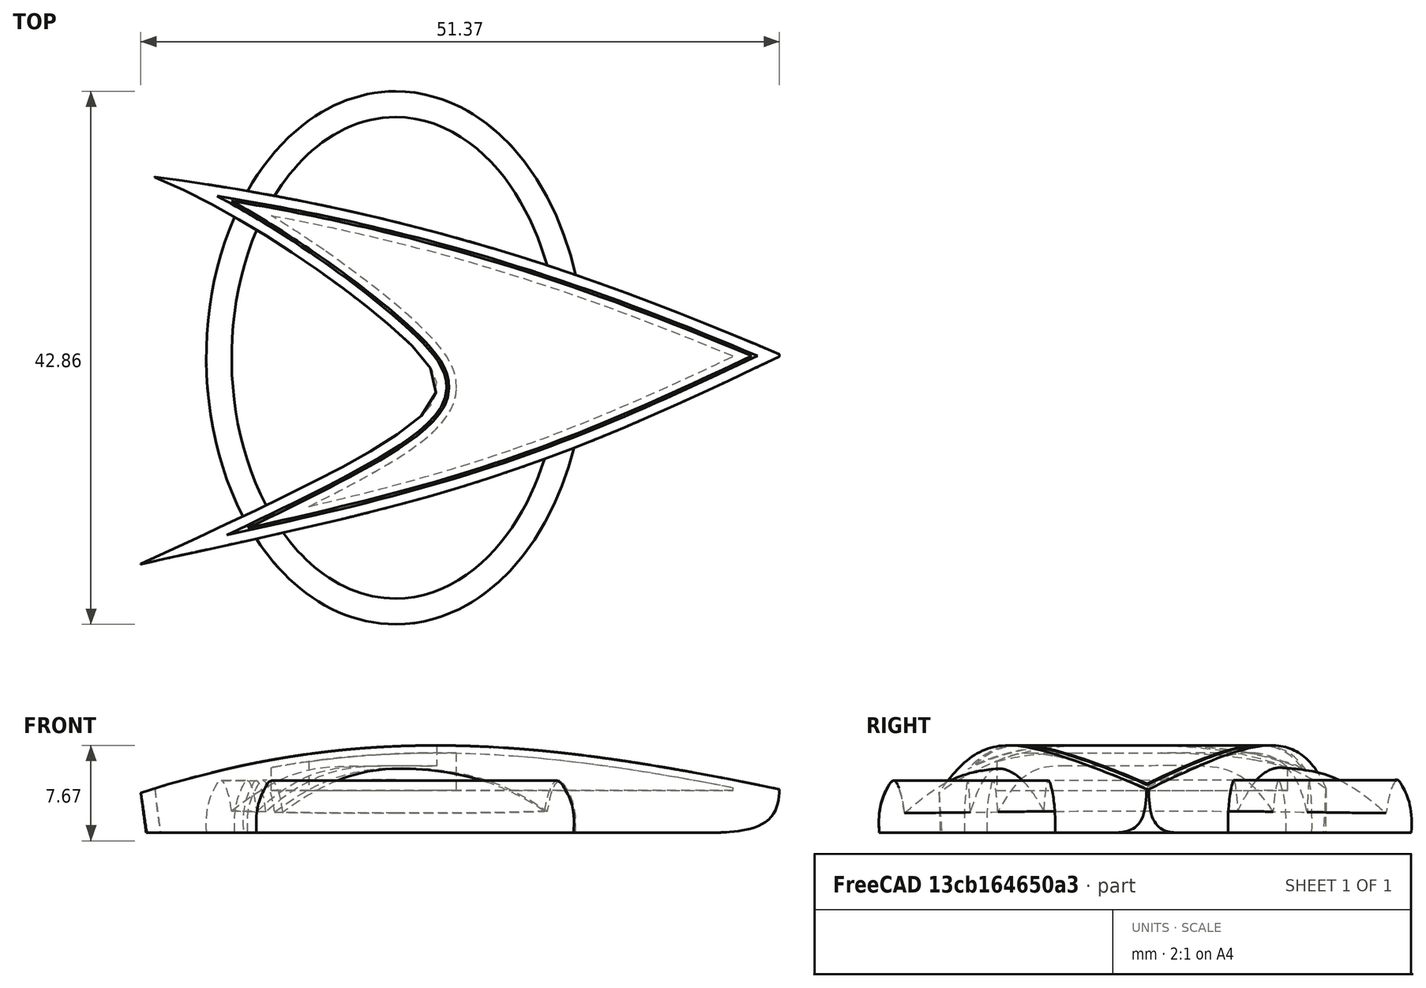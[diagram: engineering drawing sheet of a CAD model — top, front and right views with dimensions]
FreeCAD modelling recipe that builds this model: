
FCSTD DOCUMENT  (FreeCAD 0.19R23754 (Git))
Label: combadge
License: Creative Commons Attribution-NonCommercial-ShareAlike
LicenseURL: http://creativecommons.org/licenses/by-nc-sa/4.0/
objects: Sketcher::SketchObject×15, PartDesign::Pocket×4, Part::Feature×4, Part::Offset2D×3, PartDesign::Body×3, Part::Extrusion×3, PartDesign::Pad×2, PartDesign::Plane×2, Part::MultiFuse×2, Mesh::Feature×1, PartDesign::Fillet×1, PartDesign::AdditivePipe×1, PartDesign::Mirrored×1, Surface::Filling×1, Part::Cut×1, App::Part×1, PartDesign::FeatureBase×1, PartDesign::Thickness×1
note: 54 computed .brp shape members not serialized (recipe doc carries the construction recipe); baked Part::Feature solids carry a one-line shape summary decoded from their .brp

FEATURE [Mesh::Feature] TNG_BadgeFlat
  Placement = pos=(-0.244829,-0.419663,6.28091) rot=(-0.037905,0.99862,0.036356;1.53046rad)
FEATURE [Sketcher::SketchObject] Sketch  label="Ellipse"
  FullyConstrained = false
  sketch-geometry (10):
    g0: Ellipse CenterX=0 CenterY=0 CenterZ=0 NormalX=0 NormalY=0 NormalZ=1 MajorRadius=19.15 MinorRadius=12.95 AngleXU=-1.5708
    g1: LineSegment StartX=0 StartY=-19.15 StartZ=0 EndX=0 EndY=19.15 EndZ=0
    g2: LineSegment StartX=12.95 StartY=0 StartZ=0 EndX=-12.95 EndY=0 EndZ=0
    g3: GeomPoint X=0 Y=-14.1074 Z=0
    g4: GeomPoint X=0 Y=14.1074 Z=0
    g5: ArcOfEllipse CenterX=0 CenterY=0 CenterZ=0 NormalX=0 NormalY=0 NormalZ=1 MajorRadius=19.15 MinorRadius=12.95 AngleXU=1.5708 StartAngle=3.19564e-07 EndAngle=3.14159
    g6: LineSegment StartX=4.13836e-06 StartY=19.15 StartZ=0 EndX=-4.13836e-06 EndY=-19.15 EndZ=0
    g7: LineSegment StartX=-12.95 StartY=2.79852e-06 StartZ=0 EndX=12.95 EndY=-2.79852e-06 EndZ=0
    g8: GeomPoint X=3.04865e-06 Y=14.1074 Z=0
    g9: GeomPoint X=-3.04865e-06 Y=-14.1074 Z=0
  constraints (10):
    c: InternalAlignment(g1-g4 -> g0) x4
    c: Coincident(g0,g-1)
    c: Vertical(g1)
    c: DistanceY(g1,g1) = 38.3
    c: DistanceX(g2,g2) = 25.9
    c: InternalAlignment(g6-g9 -> g5) x4
    c: Coincident(g5,g-1)
    c: PointOnObject(g2,g5)
    c: Coincident(g5,g1)
    c: Coincident(g5,g1)
FEATURE [Sketcher::SketchObject] Sketch001  label="Rand"
  ExternalGeometry = -> [Sketch]
  FullyConstrained = false
  MapMode = 4
  Placement = pos=(0,0,0) rot=(0.57735,0.57735,0.57735;2.0944rad)
  Support = -> [Sketch]
  sketch-geometry (19):
    g0-g4: Circle x5 (B-spline internal-alignment scaffolding for g5; pole/knot coordinates omitted)
    g5: BSplineCurve PolesCount=10 KnotsCount=4 Degree=4 IsPeriodic=0
    g6: GeomPoint X=21.4 Y=0 Z=0
    g7: GeomPoint X=20.6644 Y=3.7658 Z=0
    g8: GeomPoint X=19.5634 Y=3.37924 Z=0
    g9: LineSegment StartX=19.15 StartY=0.882177 StartZ=0 EndX=19.15 EndY=0 EndZ=0
    g10-g14: Circle x5 (B-spline internal-alignment scaffolding for g5; pole/knot coordinates omitted)
    g15: GeomPoint X=20.5959 Y=3.86457 Z=0
    g16: GeomPoint X=19.7596 Y=3.42529 Z=0
    g17: GeomPoint X=19.15 Y=0.882177 Z=0
    g18: LineSegment StartX=19.15 StartY=0 StartZ=0 EndX=21.4 EndY=0 EndZ=0
  constraints (22):
    c: PointOnObject(g5,g-1)
    c: Weight(g0) = 1
    c: Equal(g0, g1-g4) x4
    c: InternalAlignment(g0-g4 -> g5) x5
    c: InternalAlignment(g6,g5)
    c: Coincident(g9,g5)
    c: Vertical(g9)
    c: InternalAlignment(g10,g5)
    c: Equal(g10,g0)
    c: InternalAlignment(g11,g5)
    c: Equal(g11,g0)
    c: InternalAlignment(g12,g5)
    c: Equal(g12,g0)
    c: InternalAlignment(g13,g5)
    c: Equal(g13,g0)
    c: InternalAlignment(g14,g5)
    c: Equal(g14,g0)
    c: InternalAlignment(g15,g5)
    c: InternalAlignment(g16,g5)
    c: Coincident(g18,g9)
    c: Coincident(g18,g5)
    c: Horizontal(g18)
FEATURE [Sketcher::SketchObject] Sketch006
  FullyConstrained = false
  MapMode = 5
  Support = -> [XY_Plane]
  sketch-geometry (26):
    g0: Circle CenterX=-19.5713 CenterY=14.5797 CenterZ=0 NormalX=0 NormalY=0 NormalZ=1 AngleXU=0 Radius=1.46245
    g1: Circle CenterX=-0.259309 CenterY=12.0009 CenterZ=0 NormalX=0 NormalY=0 NormalZ=1 AngleXU=0 Radius=1.46245
    g2: Circle CenterX=14.2852 CenterY=7.41686 CenterZ=0 NormalX=0 NormalY=0 NormalZ=1 AngleXU=0 Radius=1.46245
    g3: BSplineCurve PolesCount=4 KnotsCount=2 Degree=3 IsPeriodic=0
    g4: GeomPoint X=-19.5713 Y=14.5797 Z=0
    g5: GeomPoint X=31.0596 Y=0.194933 Z=0
    g6: Circle CenterX=31.0596 CenterY=0.194933 CenterZ=0 NormalX=0 NormalY=0 NormalZ=1 AngleXU=0 Radius=2
    g7: Circle CenterX=16.0165 CenterY=-6.95937 CenterZ=0 NormalX=0 NormalY=0 NormalZ=1 AngleXU=0 Radius=2
    g8: Circle CenterX=7.18268 CenterY=-10.9989 CenterZ=0 NormalX=0 NormalY=0 NormalZ=1 AngleXU=0 Radius=2.06771
    g9: BSplineCurve PolesCount=5 KnotsCount=2 Degree=4 IsPeriodic=0
    g10: GeomPoint X=31.0596 Y=0.194933 Z=0
    g11: GeomPoint X=-20.5878 Y=-16.624 Z=0
    g12: Circle CenterX=31.0596 CenterY=0.194933 CenterZ=0 NormalX=0 NormalY=0 NormalZ=1 AngleXU=0 Radius=1.44783
    g13: Circle CenterX=-7.15556 CenterY=-13.5736 CenterZ=0 NormalX=0 NormalY=0 NormalZ=1 AngleXU=0 Radius=2
    g14: Circle CenterX=-20.5878 CenterY=-16.624 CenterZ=0 NormalX=0 NormalY=0 NormalZ=1 AngleXU=0 Radius=2
    g15-g19: Circle x5 (B-spline internal-alignment scaffolding for g20; pole/knot coordinates omitted)
    g20: BSplineCurve PolesCount=7 KnotsCount=3 Degree=4 IsPeriodic=0
    g21: GeomPoint X=-19.5713 Y=14.5797 Z=0
    g22: GeomPoint X=3.29509 Y=-2.54799 Z=0
    g23: GeomPoint X=-20.5878 Y=-16.624 Z=0
    g24: Circle CenterX=-11.0843 CenterY=-12.2672 CenterZ=0 NormalX=0 NormalY=0 NormalZ=1 AngleXU=0 Radius=2
    g25: Circle CenterX=-20.5878 CenterY=-16.624 CenterZ=0 NormalX=0 NormalY=0 NormalZ=1 AngleXU=0 Radius=2
  constraints (30):
    c: Equal(g0,g2)
    c: InternalAlignment(g0,g3)
    c: InternalAlignment(g1,g3)
    c: InternalAlignment(g2,g3)
    c: InternalAlignment(g4,g3)
    c: InternalAlignment(g5,g3)
    c: Coincident(g9,g3)
    c: Weight(g6) = 2
    c: Equal(g6,g7)
    c: InternalAlignment(g6,g9)
    c: InternalAlignment(g7,g9)
    c: InternalAlignment(g8,g9)
    c: InternalAlignment(g10,g9)
    c: InternalAlignment(g11,g9)
    c: InternalAlignment(g12,g3)
    c: InternalAlignment(g13,g9)
    c: Equal(g13,g6)
    c: InternalAlignment(g14,g9)
    c: Equal(g14,g6)
    c: Coincident(g20,g3)
    c: Weight(g15) = 2
    c: Equal(g15,g16)
    c: Equal(g15,g18)
    c: Equal(g15,g19)
    c: Coincident(g20,g9)
    c: InternalAlignment(g15-g19 -> g20) x5
    c: InternalAlignment(g21-g24 -> g20) x4
    c: Equal(g24,g15)
    c: InternalAlignment(g25,g20)
    c: Equal(g25,g15)
FEATURE [PartDesign::Pad] Pad
  Direction = (1,1,1)
  Length = 10
  Length2 = 100
  Profile = -> Sketch006
  Refine = true
  Type = 0
FEATURE [Sketcher::SketchObject] Sketch007
  FullyConstrained = false
  MapMode = 5
  Placement = pos=(0,0,0) rot=(1,0,0;1.5708rad)
  Support = -> [XZ_Plane]
  sketch-geometry (20):
    g0-g3: Circle x4 (B-spline internal-alignment scaffolding for g4; pole/knot coordinates omitted)
    g4: BSplineCurve PolesCount=5 KnotsCount=2 Degree=4 IsPeriodic=0
    g5: GeomPoint X=-20.6178 Y=3.15654 Z=0
    g6: GeomPoint X=30.8704 Y=3.48185 Z=0
    g7: Circle CenterX=30.8704 CenterY=3.48185 CenterZ=0 NormalX=0 NormalY=0 NormalZ=1 AngleXU=0 Radius=1
    g8: LineSegment StartX=-20.6178 StartY=3.15654 StartZ=0 EndX=-20.6178 EndY=0 EndZ=0
    g9: LineSegment StartX=-20.6178 StartY=0 StartZ=0 EndX=25.5034 EndY=0 EndZ=0
    g10: Circle CenterX=30.8704 CenterY=3.48185 CenterZ=0 NormalX=0 NormalY=0 NormalZ=1 AngleXU=0 Radius=1
    g11: Circle CenterX=30.8704 CenterY=0 CenterZ=0 NormalX=0 NormalY=0 NormalZ=1 AngleXU=0 Radius=1.19465
    g12: Circle CenterX=25.5034 CenterY=0 CenterZ=0 NormalX=0 NormalY=0 NormalZ=1 AngleXU=0 Radius=1
    g13: BSplineCurve PolesCount=3 KnotsCount=2 Degree=2 IsPeriodic=0
    g14: GeomPoint X=30.8704 Y=3.48185 Z=0
    g15: GeomPoint X=25.5034 Y=0 Z=0
    g16: LineSegment StartX=-33.2238 StartY=22.1351 StartZ=0 EndX=44.0029 EndY=22.1351 EndZ=0
    g17: LineSegment StartX=44.0029 StartY=22.1351 StartZ=0 EndX=44.0029 EndY=-12.1343 EndZ=0
    g18: LineSegment StartX=44.0029 StartY=-12.1343 StartZ=0 EndX=-33.2238 EndY=-12.1343 EndZ=0
    g19: LineSegment StartX=-33.2238 StartY=-12.1343 StartZ=0 EndX=-33.2238 EndY=22.1351 EndZ=0
  constraints (33):
    c: Weight(g0) = 1
    c: Equal(g0,g1)
    c: Equal(g0,g2)
    c: Equal(g0,g3)
    c: InternalAlignment(g0-g3 -> g4) x4
    c: InternalAlignment(g5,g4)
    c: InternalAlignment(g6,g4)
    c: InternalAlignment(g7,g4)
    c: Equal(g7,g0)
    c: Coincident(g8,g4)
    c: Coincident(g8,g9)
    c: Horizontal(g9)
    c: Coincident(g13,g4)
    c: Weight(g10) = 1
    c: Equal(g10,g12)
    c: Coincident(g13,g9)
    c: InternalAlignment(g10,g13)
    c: InternalAlignment(g11,g13)
    c: InternalAlignment(g12,g13)
    c: InternalAlignment(g14,g13)
    c: InternalAlignment(g15,g13)
    c: PointOnObject(g8,g-1)
    c: Vertical(g8)
    c: Vertical(g11,g4)
    c: Horizontal(g11,g9)
    c: Coincident(g16,g17)
    c: Coincident(g17,g18)
    c: Coincident(g18,g19)
    c: Coincident(g19,g16)
    c: Horizontal(g16)
    c: Horizontal(g18)
    c: Vertical(g17)
    c: Vertical(g19)
FEATURE [PartDesign::Pocket] Pocket
  BaseFeature = -> Pad
  Length = 5
  Length2 = 100
  Midplane = true
  Profile = -> Sketch007
  Refine = true
  Type = 1
FEATURE [PartDesign::Fillet] Fillet
  Base = -> Pocket [Edge4,Edge12]
  BaseFeature = -> Pocket
  Radius = 0.01
  Refine = true
  SupportTransform = false
FEATURE [PartDesign::Plane] DatumPlane
  AttachmentOffset = pos=(0,0,0) rot=(0,0,1;0.017453rad)
  Length = 75.3027
  MapMode = 13
  Placement = pos=(-3.37241,-11.0335,2.22625) rot=(0.975766,0.145991,0.162998;1.59809rad)
  ResizeMode = 0
  Support = -> [Fillet]
  Width = 62.5177
FEATURE [Sketcher::SketchObject] Sketch008
  ExternalGeometry = -> [Fillet]
  FullyConstrained = false
  MapMode = 5
  Placement = pos=(-3.37241,-11.0335,2.22625) rot=(0.975766,0.145991,0.162998;1.59809rad)
  Support = -> [DatumPlane]
  sketch-geometry (4):
    g0: LineSegment StartX=-18.45 StartY=-2.08046 StartZ=0 EndX=-17.5429 EndY=-2.08046 EndZ=0
    g1: LineSegment StartX=-17.5429 StartY=-2.08046 StartZ=0 EndX=-18.032 EndY=1.64461 EndZ=0
    g2: LineSegment StartX=-18.032 StartY=1.64461 StartZ=0 EndX=-18.45 EndY=1.64461 EndZ=0
    g3: LineSegment StartX=-18.45 StartY=1.64461 StartZ=0 EndX=-18.45 EndY=-2.08046 EndZ=0
  constraints (8):
    c: Horizontal(g0)
    c: Coincident(g0,g1)
    c: Coincident(g2,g3)
    c: Vertical(g3)
    c: Coincident(g0,g3)
    c: Horizontal(g2)
    c: Coincident(g1,g2)
    c: PointOnObject(g-3,g1)
FEATURE [PartDesign::Pocket] Pocket001
  BaseFeature = -> Fillet
  Length = 5
  Length2 = 100
  Midplane = true
  Profile = -> Sketch008
  Refine = true
  Type = 1
FEATURE [PartDesign::Plane] DatumPlane001
  Length = 72.9682
  MapMode = 13
  Placement = pos=(-2.70782,9.73491,2.3319) rot=(0.980809,-0.137865,-0.137865;1.59017rad)
  ResizeMode = 0
  Support = -> [Pocket001]
  Width = 61.1217
FEATURE [Sketcher::SketchObject] Sketch009
  ExternalGeometry = -> [Pocket001]
  FullyConstrained = false
  MapMode = 5
  Placement = pos=(-2.70782,9.73491,2.3319) rot=(0.980809,-0.137865,-0.137865;1.59017rad)
  Support = -> [DatumPlane001]
  sketch-geometry (9):
    g0: LineSegment StartX=-17.3861 StartY=1.7491 StartZ=0 EndX=-18.1476 EndY=1.7491 EndZ=0
    g1: LineSegment StartX=-18.1476 StartY=1.7491 StartZ=0 EndX=-18.1476 EndY=-2.7517 EndZ=0
    g2: LineSegment StartX=-18.1476 StartY=-2.7517 StartZ=0 EndX=-16.7869 EndY=-2.7517 EndZ=0
    g3: Circle CenterX=-17.3861 CenterY=1.7491 CenterZ=0 NormalX=0 NormalY=0 NormalZ=1 AngleXU=0 Radius=1
    g4: Circle CenterX=-17.2032 CenterY=-0.435236 CenterZ=0 NormalX=0 NormalY=0 NormalZ=1 AngleXU=0 Radius=1
    g5: Circle CenterX=-16.7869 CenterY=-2.7517 CenterZ=0 NormalX=0 NormalY=0 NormalZ=1 AngleXU=0 Radius=1
    g6: BSplineCurve PolesCount=3 KnotsCount=2 Degree=2 IsPeriodic=0
    g7: GeomPoint X=-17.3861 Y=1.7491 Z=0
    g8: GeomPoint X=-16.7869 Y=-2.7517 Z=0
  constraints (15):
    c: Horizontal(g0)
    c: Coincident(g0,g1)
    c: Vertical(g1)
    c: Coincident(g1,g2)
    c: Horizontal(g2)
    c: Coincident(g6,g0)
    c: Weight(g3) = 1
    c: Equal(g3,g4)
    c: Equal(g3,g5)
    c: Coincident(g6,g2)
    c: InternalAlignment(g3,g6)
    c: InternalAlignment(g4,g6)
    c: InternalAlignment(g5,g6)
    c: InternalAlignment(g7,g6)
    c: InternalAlignment(g8,g6)
FEATURE [Sketcher::SketchObject] Sketch010
  FullyConstrained = true
  Placement = pos=(0,0,0) rot=(1,0,0;1.5708rad)
  sketch-geometry (8):
    g0-g3: Circle x4 (B-spline internal-alignment scaffolding for g4; pole/knot coordinates omitted)
    g4: BSplineCurve PolesCount=4 KnotsCount=2 Degree=3 IsPeriodic=0
    g5: GeomPoint X=14.26 Y=0.8 Z=0
    g6: GeomPoint X=0 Y=5.38 Z=0
    g7: LineSegment StartX=14.26 StartY=0.8 StartZ=0 EndX=14.26 EndY=0 EndZ=0
  constraints (14):
    c: Weight(g0) = 0.7
    c: Equal(g0,g3)
    c: PointOnObject(g4,g-2)
    c: InternalAlignment(g0-g3 -> g4) x4
    c: InternalAlignment(g5,g4)
    c: InternalAlignment(g6,g4)
    c: Horizontal(g4,g2)
    c: DistanceY(g-1,g4) = 5.38
    c: DistanceY(g-1,g4) = 0.8
    c: Coincident(g7,g4)
    c: PointOnObject(g7,g-1)
    c: Vertical(g7)
    c: Block(g4)
    c: DistanceX(g-1,g7) = 14.26
FEATURE [Sketcher::SketchObject] Sketch011
  ExternalGeometry = -> [Sketch010]
  FullyConstrained = true
  Placement = pos=(0,0,0) rot=(0.57735,0.57735,0.57735;2.0944rad)
  sketch-geometry (8):
    g0-g3: Circle x4 (B-spline internal-alignment scaffolding for g4; pole/knot coordinates omitted)
    g4: BSplineCurve PolesCount=4 KnotsCount=2 Degree=3 IsPeriodic=0
    g5: GeomPoint X=1.2e-15 Y=5.38 Z=0
    g6: GeomPoint X=20.23 Y=0.8 Z=0
    g7: LineSegment StartX=20.23 StartY=0.8 StartZ=0 EndX=20.23 EndY=0 EndZ=0
  constraints (14):
    c: Weight(g0) = 1
    c: Equal(g0,g3)
    c: InternalAlignment(g0-g3 -> g4) x4
    c: InternalAlignment(g5,g4)
    c: InternalAlignment(g6,g4)
    c: Horizontal(g1,g4)
    c: Coincident(g7,g4)
    c: PointOnObject(g7,g-1)
    c: Vertical(g7)
    c: Horizontal(g1,g2)
    c: DistanceX(g-1,g7) = 20.23
    c: Coincident(g4,g-4)
    c: Horizontal(g-3,g4)
    c: Block(g4)
FEATURE [Sketcher::SketchObject] Sketch012
  ExternalGeometry = -> [Sketch011,Sketch010]
  FullyConstrained = false
  Placement = pos=(0,0,0.8) rot=(0,0,1;0rad)
  sketch-geometry (3):
    g0: BSplineCurve PolesCount=9 KnotsCount=2 Degree=8 IsPeriodic=0
    g1: GeomPoint X=0 Y=14.3494 Z=0
    g2: GeomPoint X=0 Y=-14.3494 Z=0
  constraints (3):
    c: Coincident(g0,g-4)
    c: Coincident(g0,g-3)
    c: Block(g0)
FEATURE [Part::Offset2D] Offset2D
  Fill = false
  Intersection = false
  Join = 0
  Mode = 1
  Placement = pos=(0,0,8) rot=(0,0,1;0rad)
  SelfIntersection = false
  Source = -> Sketch006
  Value = -1.6
FEATURE [Part::Offset2D] Offset2D001
  Fill = false
  Intersection = false
  Join = 0
  Mode = 1
  Placement = pos=(0,0,8) rot=(0,0,1;0rad)
  SelfIntersection = false
  Source = -> Sketch006
  Value = -0.8
FEATURE [Part::Offset2D] Offset2D002
  Fill = false
  Intersection = false
  Join = 0
  Mode = 1
  Placement = pos=(0,0,3.4) rot=(0,0,1;0rad)
  SelfIntersection = false
  Source = -> Sketch006
  Value = -1
FEATURE [PartDesign::Pocket] Pocket002
  BaseFeature = -> Pocket001
  Length = 5
  Length2 = 100
  Midplane = true
  Profile = -> Sketch009
  Refine = true
  Type = 0
FEATURE [PartDesign::Body] Body  label="Pfeil"
  Group = -> [Sketch006,Pad,Sketch007,Pocket,Fillet,DatumPlane,Sketch008,Pocket001,DatumPlane001,Sketch009,Pocket002]
  Origin = -> Origin
  Tip = -> Pocket002
FEATURE [Part::Extrusion] Extrude005
  Base = -> Offset2D
  Dir = (0,0,-1)
  DirMode = 2
  FaceMakerClass = Part::FaceMakerBullseye
  LengthFwd = 7
  LengthRev = 0
  Solid = true
  Symmetric = false
FEATURE [Part::Extrusion] Extrude007
  Base = -> Offset2D001
  Dir = (0,0,-1)
  DirMode = 2
  FaceMakerClass = Part::FaceMakerBullseye
  LengthFwd = 5
  LengthRev = 0
  Solid = true
  Symmetric = false
FEATURE [Part::MultiFuse] Fusion001  label="Cutout"
  Refine = true
  Shapes = -> [Extrude007,Extrude005]
FEATURE [Sketcher::SketchObject] MirroredSketch  label="Rand 2"
  FullyConstrained = false
  Placement = pos=(0,0,0) rot=(0.57735,0.57735,0.57735;2.0944rad)
  sketch-geometry (19):
    g0-g4: Circle x5 (B-spline internal-alignment scaffolding for g5; pole/knot coordinates omitted)
    g5: BSplineCurve PolesCount=10 KnotsCount=4 Degree=4 IsPeriodic=0
    g6: GeomPoint X=-21.4 Y=0 Z=0
    g7: GeomPoint X=-20.6644 Y=3.7658 Z=0
    g8: GeomPoint X=-19.5634 Y=3.37924 Z=0
    g9: LineSegment StartX=-19.15 StartY=0.882177 StartZ=0 EndX=-19.15 EndY=0 EndZ=0
    g10-g14: Circle x5 (B-spline internal-alignment scaffolding for g5; pole/knot coordinates omitted)
    g15: GeomPoint X=-20.5959 Y=3.86457 Z=0
    g16: GeomPoint X=-19.7596 Y=3.42529 Z=0
    g17: GeomPoint X=-19.15 Y=0.882177 Z=0
    g18: LineSegment StartX=-19.15 StartY=0 StartZ=0 EndX=-21.4 EndY=0 EndZ=0
  constraints (21):
    c: Weight(g0) = 1
    c: Equal(g0, g1-g4) x4
    c: InternalAlignment(g0-g4 -> g5) x5
    c: InternalAlignment(g6,g5)
    c: Coincident(g9,g5)
    c: Vertical(g9)
    c: InternalAlignment(g10,g5)
    c: Equal(g10,g0)
    c: InternalAlignment(g11,g5)
    c: Equal(g11,g0)
    c: InternalAlignment(g12,g5)
    c: Equal(g12,g0)
    c: InternalAlignment(g13,g5)
    c: Equal(g13,g0)
    c: InternalAlignment(g14,g5)
    c: Equal(g14,g0)
    c: InternalAlignment(g15,g5)
    c: InternalAlignment(g16,g5)
    c: Coincident(g18,g9)
    c: Coincident(g18,g5)
    c: Horizontal(g18)
FEATURE [PartDesign::AdditivePipe] AdditivePipe
  AuxilleryCurvelinear = true
  AuxillerySpineTangent = false
  Binormal = (0,0,0)
  Mode = 2
  Profile = -> Sketch001
  Refine = true
  Sections = -> [MirroredSketch]
  Spine = -> Sketch [Edge1]
  SpineTangent = false
  Transformation = 1
  Transition = 0
FEATURE [PartDesign::Mirrored] Mirrored
  BaseFeature = -> AdditivePipe
  MirrorPlane = -> YZ_Plane001
  Originals = -> [AdditivePipe]
  Refine = true
FEATURE [PartDesign::Body] Body001  label="Rand"
  Group = -> [Sketch,Sketch001,AdditivePipe,Mirrored,MirroredSketch]
  Origin = -> Origin001
  Tip = -> Mirrored
FEATURE [Sketcher::SketchObject] MirroredSketch001  label="Mirrored Sketch011"
  FullyConstrained = false
  Placement = pos=(0,0,0) rot=(0.57735,0.57735,0.57735;2.0944rad)
  sketch-geometry (8):
    g0-g3: Circle x4 (B-spline internal-alignment scaffolding for g4; pole/knot coordinates omitted)
    g4: BSplineCurve PolesCount=4 KnotsCount=2 Degree=3 IsPeriodic=0
    g5: GeomPoint X=-1.2e-15 Y=5.38 Z=0
    g6: GeomPoint X=-20.23 Y=0.8 Z=0
    g7: LineSegment StartX=-20.23 StartY=0.8 StartZ=0 EndX=-20.23 EndY=0 EndZ=0
  constraints (8):
    c: Weight(g0) = 1
    c: Equal(g0,g3)
    c: InternalAlignment(g0-g3 -> g4) x4
    c: InternalAlignment(g5,g4)
    c: InternalAlignment(g6,g4)
    c: Coincident(g7,g4)
    c: Vertical(g7)
    c: Block(g4)
FEATURE [Sketcher::SketchObject] MirroredSketch002  label="Mirrored Sketch010"
  FullyConstrained = false
  Placement = pos=(0,0,0) rot=(1,0,0;1.5708rad)
  sketch-geometry (8):
    g0-g3: Circle x4 (B-spline internal-alignment scaffolding for g4; pole/knot coordinates omitted)
    g4: BSplineCurve PolesCount=4 KnotsCount=2 Degree=3 IsPeriodic=0
    g5: GeomPoint X=-14.26 Y=0.8 Z=0
    g6: GeomPoint X=0 Y=5.38 Z=0
    g7: LineSegment StartX=-14.26 StartY=0.8 StartZ=0 EndX=-14.26 EndY=0 EndZ=0
  constraints (8):
    c: Weight(g0) = 0.7
    c: Equal(g0,g3)
    c: InternalAlignment(g0-g3 -> g4) x4
    c: InternalAlignment(g5,g4)
    c: InternalAlignment(g6,g4)
    c: Coincident(g7,g4)
    c: Vertical(g7)
    c: Block(g4)
FEATURE [Sketcher::SketchObject] MirroredSketch003  label="Mirrored Sketch012 c"
  FullyConstrained = true
  Placement = pos=(0,0,0.8) rot=(0,0,1;0rad)
  sketch-geometry (1):
    g0: BSplineCurve PolesCount=9 KnotsCount=2 Degree=8 IsPeriodic=0
  constraints (1):
    c: Block(g0)
FEATURE [Sketcher::SketchObject] MirroredSketch004  label="Mirrored Skatch012 b"
  FullyConstrained = true
  Placement = pos=(0,0,0.8) rot=(0,0,1;0rad)
  sketch-geometry (1):
    g0: BSplineCurve PolesCount=9 KnotsCount=2 Degree=8 IsPeriodic=0
  constraints (1):
    c: Block(g0)
FEATURE [Sketcher::SketchObject] MirroredSketch005  label="Mirrored Sketch012 a"
  FullyConstrained = true
  Placement = pos=(0,0,0.8) rot=(0,0,1;0rad)
  sketch-geometry (1):
    g0: BSplineCurve PolesCount=9 KnotsCount=2 Degree=8 IsPeriodic=0
  constraints (1):
    c: Block(g0)
FEATURE [Surface::Filling] Surface002
  Anisotropy = false
  BoundaryEdges = -> [MirroredSketch004,Sketch012,MirroredSketch003,MirroredSketch005]
  BoundaryOrder = [0,0,0,0]
  Degree = 3
  Iterations = 2
  MaximumDegree = 8
  MaximumSegments = 9
  PointsOnCurve = 15
  TolAngular = 0.01
  TolCurvature = 0.1
  Tolerance2d = 1e-05
  Tolerance3d = 0.0001
  UnboundEdges = -> [Sketch011,Sketch010,MirroredSketch001,MirroredSketch002]
  UnboundOrder = [0,0,0,0]
FEATURE [Part::Feature] Wire001
  shape: bbox 28.53 x 40.47 x 0.007226 mm, 0 faces, 0 solids (baked)
FEATURE [Part::Extrusion] Extrude013
  Base = -> Wire001
  Dir = (0,0,-1)
  DirMode = 2
  FaceMakerClass = Part::FaceMakerBullseye
  LengthFwd = 0.8
  LengthRev = 0
  Solid = false
  Symmetric = false
FEATURE [Part::Feature] Face001
  shape: bbox 31.37 x 44.51 x 2e-07 mm, 1 faces, 0 solids (baked)
FEATURE [Part::Feature] Solid001  label="Dom"
  shape: bbox 31.38 x 44.52 x 22.36 mm, 6 faces (baked)
FEATURE [Part::MultiFuse] Fusion
  Refine = true
  Shapes = -> [Body,Body001,Solid001]
FEATURE [Part::Cut] Cut  label="Körper"
  Base = -> Fusion
  Refine = true
  Tool = -> Fusion001
FEATURE [Part::Feature] Shell
  shape: bbox 31.38 x 44.52 x 22.36 mm, 6 faces, 0 solids (baked)
FEATURE [App::Part] Part  label="Dombau"
  Group = -> [Shell,Face001,Surface002,Wire001,Extrude013,MirroredSketch001,MirroredSketch002,MirroredSketch003,MirroredSketch004,MirroredSketch005,Sketch010,Sketch011,Sketch012]
  Origin = -> Origin003
FEATURE [PartDesign::FeatureBase] BaseFeature
  BaseFeature = -> Offset2D002
FEATURE [PartDesign::Pad] Pad001
  BaseFeature = -> BaseFeature
  Direction = (1,1,1)
  Length = 10
  Length2 = 100
  Profile = -> Offset2D002
  Refine = true
  Reversed = true
  Type = 0
FEATURE [PartDesign::Pocket] Pocket005
  BaseFeature = -> Pad001
  Length = 5
  Length2 = 100
  Midplane = true
  Profile = -> Sketch007
  Refine = true
  Type = 1
FEATURE [PartDesign::Thickness] Thickness
  Base = -> Pocket005 [Face2]
  BaseFeature = -> Pocket005
  Intersection = false
  Join = 0
  Mode = 0
  Refine = true
  Reversed = true
  SupportTransform = false
  Value = 0.6
FEATURE [PartDesign::Body] Body002  label="Einsatz"
  BaseFeature = -> Offset2D002
  Group = -> [BaseFeature,Pad001,Pocket005,Thickness]
  Origin = -> Origin002
  Tip = -> Thickness
